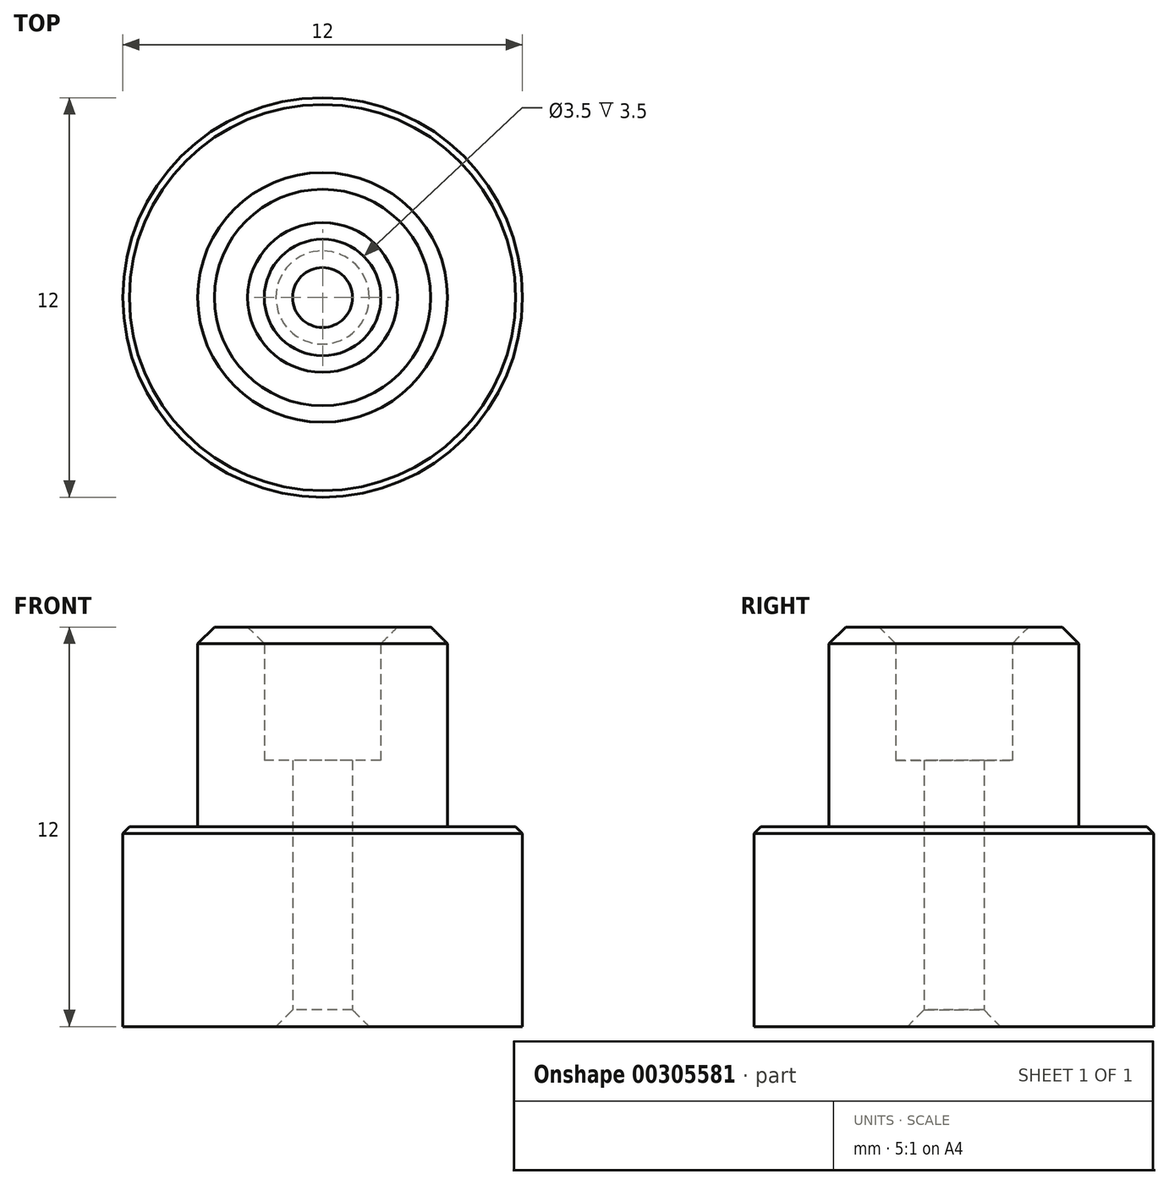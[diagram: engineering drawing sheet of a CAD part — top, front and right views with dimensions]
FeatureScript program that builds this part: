
annotation { "Feature Type Name" : "Feature", "Feature Type Description" : "" }
export const myFeature = defineFeature(function(context is Context, id is Id, definition is map)
    precondition{}
    {
        {
            var Q0;
            Q0=qCreatedBy(makeId("Top.planeOp"),FACE);
            var sketch = newSketch(context, id + "F0", { "sketchPlane" : qUnion([Q0])});
            skCircle(sketch, "E0", {"center": v(0, 0) * mm, "radius": 3.75 * mm});
            skCircle(sketch, "E1", {"center": v(0, 0) * mm, "radius": 6 * mm});
            skCircle(sketch, "E2", {"center": v(0, 0) * mm, "radius": 0.9 * mm});
            skCircle(sketch, "E3", {"center": v(0, 0) * mm, "radius": 1.75 * mm});
            skSolve(sketch);
        }
        {
            var Q0;
            Q0=makeQuery(id+"F0.imprint","IMPRINT",FACE,{"disambiguationData":[TD([[makeQuery(id+"F0.imprint","IMPRINT",EDGE,{"derivedFrom":sQuery(id+"F0.wireOp",EDGE,"E0")}),1.0]])]});
            var Q1;
            Q1=makeQuery(id+"F0.imprint","IMPRINT",FACE,{"disambiguationData":[TD([[makeQuery(id+"F0.imprint","IMPRINT",EDGE,{"derivedFrom":sQuery(id+"F0.wireOp",EDGE,"E2")}),-1.0]])]});
            extrude(context, id + "F1", {"entities" : qUnion([Q0, Q1]), "depth" : 6 * mm});
        }
        {
            var Q0;
            Q0=makeQuery(id+"F0.imprint","IMPRINT",FACE,{"disambiguationData":[TD([[makeQuery(id+"F0.imprint","IMPRINT",EDGE,{"derivedFrom":sQuery(id+"F0.wireOp",EDGE,"E0")}),-1.0]])]});
            var Q1;
            Q1=makeQuery(id+"F1.opExtrude","CAP_FACE",FACE,{"disambiguationData":[OSD([sQuery(id+"F0.wireOp",EDGE,"E0")])],"isStart":false});
            extrude(context, id + "F2", {"entities" : qUnion([Q0, Q1]), "operationType" : NewBodyOperationType.ADD, "depth" : 6 * mm});
        }
        {
            var Q0;
            Q0=makeQuery(id+"F0.imprint","IMPRINT",FACE,{"disambiguationData":[TD([[makeQuery(id+"F0.imprint","IMPRINT",EDGE,{"derivedFrom":sQuery(id+"F0.wireOp",EDGE,"E2")}),-1.0]])]});
            var Q1;
            Q1=makeQuery(id+"F2.opExtrude","CAP_FACE",FACE,{"disambiguationData":[OSD([sQuery(id+"F0.wireOp",EDGE,"E0"),sQuery(id+"F0.wireOp",EDGE,"E2")])],"isStart":false});
            extrude(context, id + "F3", {"entities" : qUnion([Q0]), "operationType" : NewBodyOperationType.REMOVE, "depth" : 14 * mm, "hasSecondDirection" : true, "secondDirectionOppositeDirection" : false, "secondDirectionBoundEntityFace" : qUnion([Q1]), "secondDirectionDepth" : 8 * mm});
        }
        {
            var Q0;
            Q0=makeQuery(id+"F1.opExtrude","CAP_EDGE",EDGE,{"disambiguationData":[OSD([sQuery(id+"F0.wireOp",EDGE,"E2")])],"isStart":true});
            chamfer(context, id + "F4", {"entities" : qUnion([Q0]), "width" : 0.5 * mm, "tangentPropagation" : true});
        }
        {
            var Q0;
            Q0=makeQuery(id+"F2.opExtrude","CAP_EDGE",EDGE,{"disambiguationData":[OSD([sQuery(id+"F0.wireOp",EDGE,"E1")])],"isStart":false});
            chamfer(context, id + "F5", {"entities" : qUnion([Q0]), "width" : 0.2 * mm, "tangentPropagation" : true});
        }
        {
            var Q0;
            {var subQ0=sQuery(id+"F0.wireOp",EDGE,"E0");Q0=makeQuery(id+"F2.opExtrude","CAP_EDGE",EDGE,{"disambiguationData":[OSD([subQ0]),TDD([makeQuery(id+"F1.opExtrude","CAP_EDGE",EDGE,{"disambiguationData":[OSD([subQ0])],"isStart":false})])],"isStart":false});}
            var Q1;
            Q1=makeQuery(id+"F2.opExtrude","CAP_FACE",FACE,{"disambiguationData":[OSD([sQuery(id+"F0.wireOp",EDGE,"E0"),sQuery(id+"F0.wireOp",EDGE,"E2")])],"isStart":false});
            chamfer(context, id + "F6", {"entities" : qUnion([Q0, Q1]), "width" : 0.5 * mm, "tangentPropagation" : true});
        }
    });
